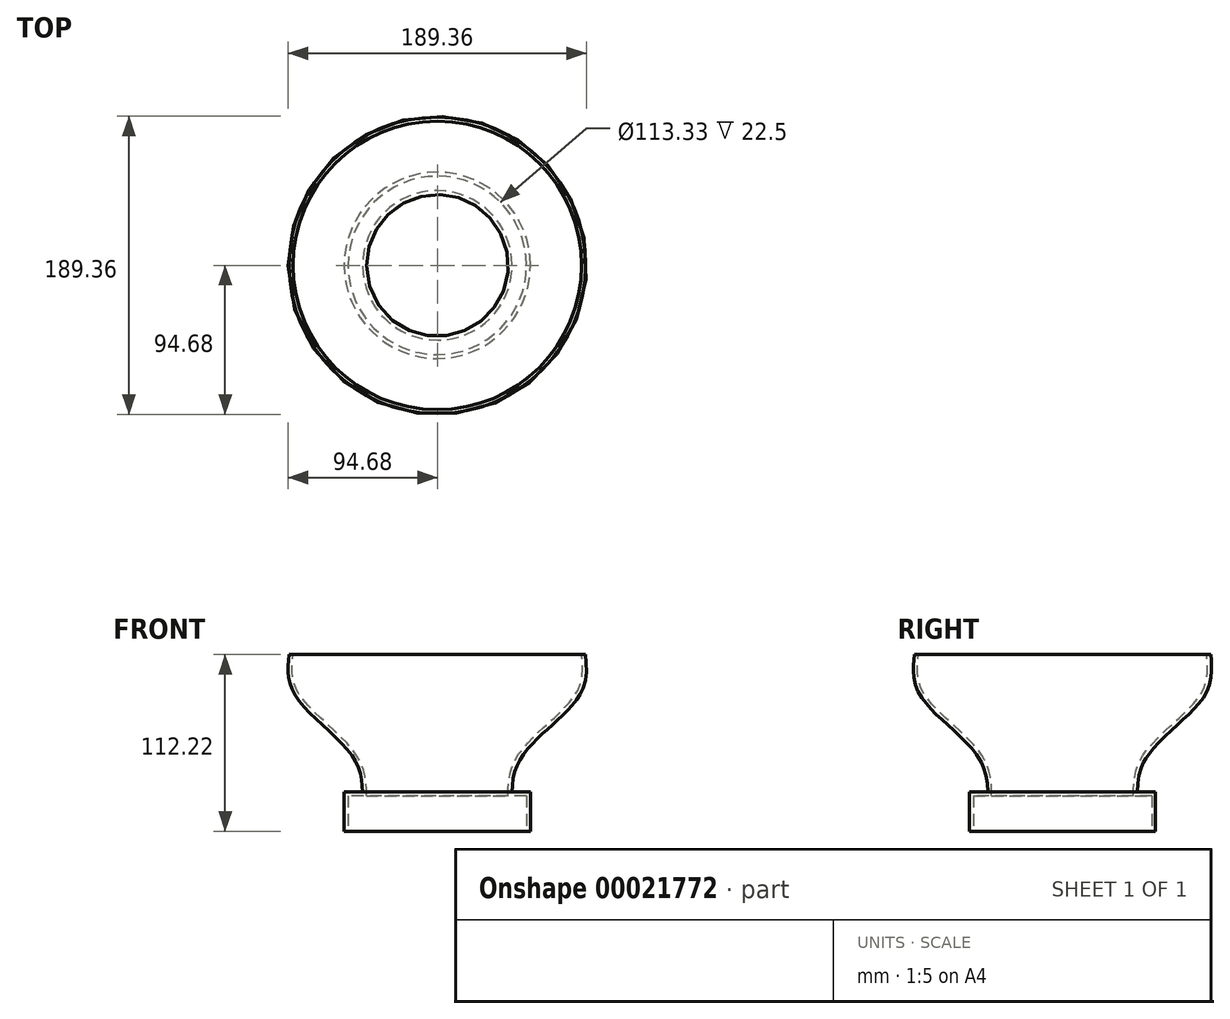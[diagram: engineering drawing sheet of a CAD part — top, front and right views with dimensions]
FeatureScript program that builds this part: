
annotation { "Feature Type Name" : "Feature", "Feature Type Description" : "" }
export const myFeature = defineFeature(function(context is Context, id is Id, definition is map)
    precondition{}
    {
        {
            var Q0;
            Q0=qCreatedBy(makeId("Top.planeOp"),FACE);
            var sketch = newSketch(context, id + "F0", { "sketchPlane" : qUnion([Q0])});
            skCircle(sketch, "E0", {"center": v(0, 0) * mm, "radius": 59.17 * mm});
            skSolve(sketch);
        }
        {
            var Q0;
            Q0 = qSketchRegion(id + "F0", true);
            extrude(context, id + "F1", {"entities" : qUnion([Q0]), "depth" : 25 * mm});
        }
        {
            var Q0;
            Q0=qCreatedBy(makeId("Front.planeOp"),FACE);
            var sketch = newSketch(context, id + "F2", { "sketchPlane" : qUnion([Q0])});
            skFitSpline(sketch, "E1", {"points": [v(-47.59, 18.08) * mm, v(-53.4, 46.97) * mm, v(-90.2, 86.03) * mm, v(-94.14, 112.22) * mm], "startDerivative": vector(2.44, 94.9) * mm, "endDerivative": vector(8, 90.08) * mm});
            skLineSegment(sketch, "E2", {"start": v(-47.59, 18.08) * mm, "end": v(0, 18.08) * mm});
            skLineSegment(sketch, "E3", {"start": v(0, 18.08) * mm, "end": v(0, 112.22) * mm});
            skLineSegment(sketch, "E4", {"start": v(0, 112.22) * mm, "end": v(-94.14, 112.22) * mm});
            skSolve(sketch);
        }
        {
            var Q0;
            Q0 = qSketchRegion(id + "F2", true);
            var Q1;
            Q1=sQuery(id+"F2.wireOp",EDGE,"E3");
            revolve(context, id + "F3", {"operationType" : NewBodyOperationType.ADD, "entities" : qUnion([Q0]), "axis" : qUnion([Q1]), "revolveType" : RevolveType.FULL});
        }
        {
            var Q0;
            Q0=makeQuery(id+"F3.opRevolve","SWEPT_FACE",FACE,{"disambiguationData":[OSD([sQuery(id+"F2.wireOp",EDGE,"E4")])]});
            var Q1;
            Q1=makeQuery(id+"F1.opExtrude","CAP_FACE",FACE,{"disambiguationData":[OSD([sQuery(id+"F0.wireOp",EDGE,"E0")])],"isStart":true});
            shell(context, id + "F4", {"entities" : qUnion([Q0, Q1]), "thickness" : 2.5 * mm});
        }
    });
